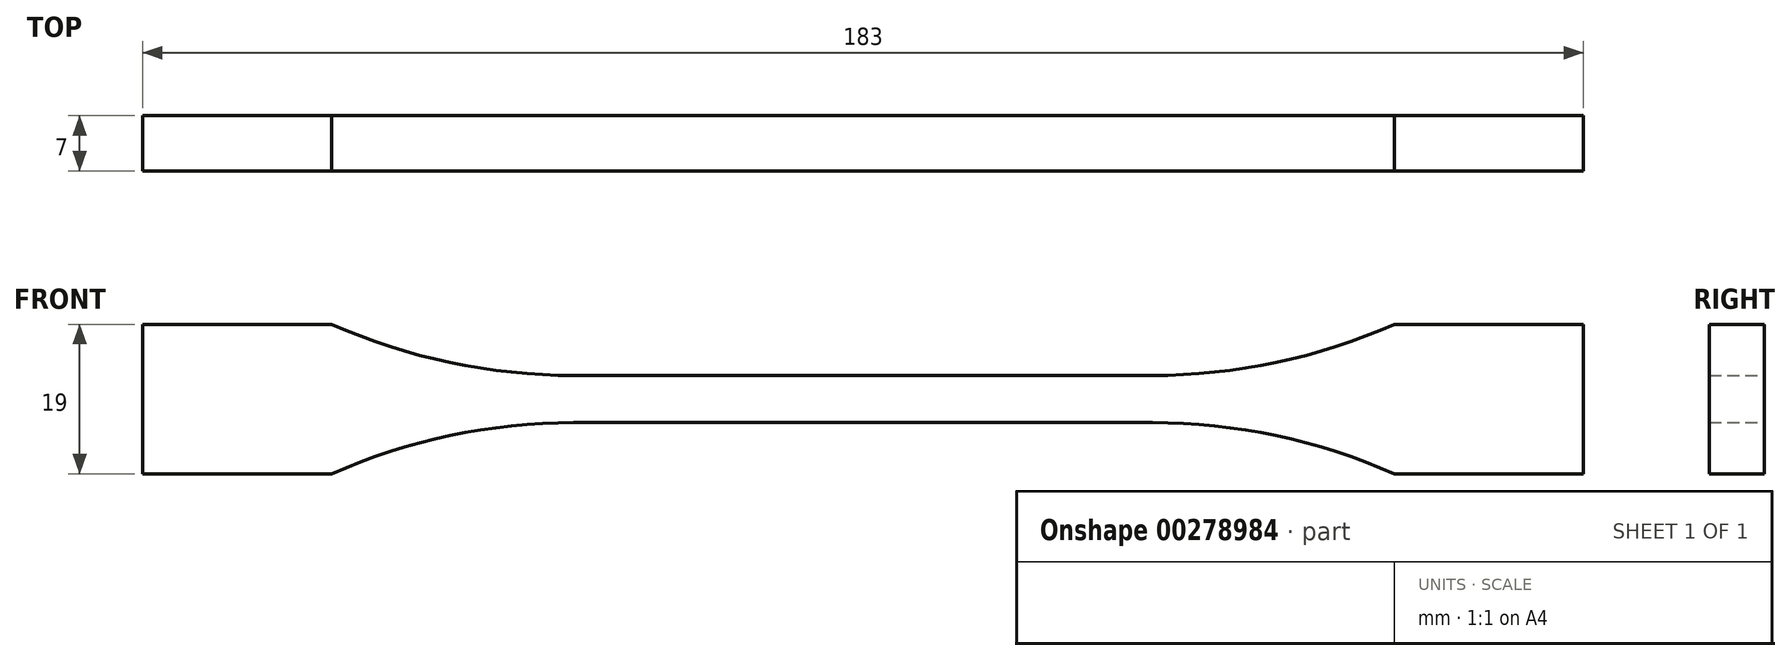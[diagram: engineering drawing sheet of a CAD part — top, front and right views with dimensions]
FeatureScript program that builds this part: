
annotation { "Feature Type Name" : "Feature", "Feature Type Description" : "" }
export const myFeature = defineFeature(function(context is Context, id is Id, definition is map)
    precondition{}
    {
        {
            var Q0;
            Q0=qCreatedBy(makeId("Front.planeOp"),FACE);
            var sketch = newSketch(context, id + "F0", { "sketchPlane" : qUnion([Q0])});
            skLineSegment(sketch, "E0", {"start": v(0, 3) * mm, "end": v(36.75, 3) * mm});
            skArc(sketch, "E1", {"start": v(36.75, 3) * mm, "mid": v(52.46, 4.64) * mm, "end": v(67.5, 9.5) * mm});
            skLineSegment(sketch, "E2", {"start": v(67.5, 9.5) * mm, "end": v(91.5, 9.5) * mm});
            skLineSegment(sketch, "E3.MirrorCS", {"start": v(67.5, -9.5) * mm, "end": v(91.5, -9.5) * mm});
            skLineSegment(sketch, "E4.MirrorCS", {"start": v(0, -3) * mm, "end": v(36.75, -3) * mm});
            skArc(sketch, "E5.MirrorCS", {"start": v(36.75, -3) * mm, "mid": v(52.46, -4.64) * mm, "end": v(67.5, -9.5) * mm});
            skArc(sketch, "E6.MirrorCS", {"start": v(-36.75, -3) * mm, "mid": v(-52.46, -4.64) * mm, "end": v(-67.5, -9.5) * mm});
            skLineSegment(sketch, "E7.MirrorCS", {"start": v(0, 3) * mm, "end": v(-36.75, 3) * mm});
            skArc(sketch, "E8.MirrorCS", {"start": v(-36.75, 3) * mm, "mid": v(-52.46, 4.64) * mm, "end": v(-67.5, 9.5) * mm});
            skLineSegment(sketch, "E9.MirrorCS", {"start": v(-67.5, -9.5) * mm, "end": v(-91.5, -9.5) * mm});
            skLineSegment(sketch, "E10.MirrorCS", {"start": v(0, -3) * mm, "end": v(-36.75, -3) * mm});
            skLineSegment(sketch, "E11.MirrorCS", {"start": v(-67.5, 9.5) * mm, "end": v(-91.5, 9.5) * mm});
            skLineSegment(sketch, "E12", {"start": v(-91.5, 9.5) * mm, "end": v(-91.5, -9.5) * mm});
            skLineSegment(sketch, "E13", {"start": v(91.5, 9.5) * mm, "end": v(91.5, -9.5) * mm});
            skSolve(sketch);
        }
        {
            var Q0;
            Q0=makeQuery(id+"F0.imprint","IMPRINT",FACE,{"disambiguationData":[TD([[makeQuery(id+"F0.imprint","IMPRINT",EDGE,{"derivedFrom":sQuery(id+"F0.wireOp",EDGE,"E0")}),-1.0]])]});
            extrude(context, id + "F1", {"entities" : qUnion([Q0]), "endBound" : BoundingType.SYMMETRIC, "depth" : 7 * mm});
        }
    });
